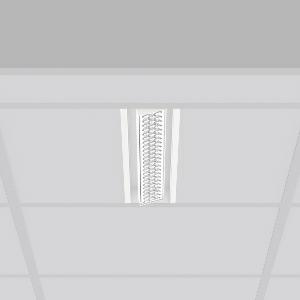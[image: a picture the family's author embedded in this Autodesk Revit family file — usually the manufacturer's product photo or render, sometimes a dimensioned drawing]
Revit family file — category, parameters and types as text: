
# Revit family: tx-move_901729_002_3_e311
name_source: partatom
category: Lighting Fixtures
units: mm (PartAtom-declared; Revit-internal decimal feet)

## family parameters
Cut with Voids When Loaded = No
Host = Face
Light Source = No
Part Type = Normal
Room Calculation Point = No
Round Connector Dimension = Use Diameter
Shared = No

## types (1)
- MultiLumen 1 (1 x LED Modul 835, 2950 lm, 3500)
    Apparent Load = 18 VA
    CIE Flux Codes = 77 96 99 100 100
    Color Rendering = 80
    Color Temperature = 3500
    Default Elevation = 1800 mm
    Description = Series: TX-MOVE
Einlege/Einbau-Flächenstrahler. Housing: sheet steel, powder-coated. Swivel range: 90°. High-efficiency LED units with optimum light control thanks to clear plastic (PC) lens optics. Spezielle Mikrostrukturen reduzieren Gelbsaum. Symmetrical light distribution. Suitable for laying in grid ceiling module 625. Connected converter included in separate gearbox.Suitable for through-wiring.MultiLumen: Luminous flux adjustable in 3 steps. Accessories: Mounting frame for installation in suspended ceilings. Environmentally friendly and resource-saving due to replaceable and recyclable components. 
Colour: traffic white, matt (RAL 9016)
Length: 622 mm
Width: 116 mm
Height: 39 mm
Cut-out length: 602 mm
Cut-out width: 98 mm
Recess height: 100 mm
Lamp: LED
Socket: without socket
Colour temperature: 3500K
Colour rendering index (CRI): 80
System power: 18 W
Rated luminous flux: 2950 lm
Luminous efficiency: 164 lm/W
System power 2: 26 W
Rated luminous flux 2: 4050 lm
Luminous efficiency 2: 156 lm/W
System power 3: 39 W
Rated luminous flux 3: 5700 lm
Luminous efficiency 3: 146 lm/W
Control gear: Regulated power supply
Protection class: I
Type of protection: IP 20
    Height = 0 mm  [stored 0 ft]
    Lamp = 1 x LED Modul 835
    Lamp Light Flux = 2950 lm
    Lamp count = 1
    Length = 622 mm
    Lifetime = 50000 h
    Luminous efficacy = 164 lm/W
    Manufacturer = RZB
    ModVariant = No
    Model = 901729.002.3
    Mounting Place = Ceiling, Wall
    Mounting Type = Recessed
    Number of Poles = 1
    OnlyDefault = Yes
    Power Factor = 1
    Product Name = TX-MOVE
    Product group = Recessed projectors
    ProductGroupID = 401
    Protection Class = Protection class I
    Protection Degree = IP 20
    RLX_Detail_Level = 1
    RLX_Emergency_Light_Flux = 0 lm
    RLX_Emergency_Type = 0
    RLX_Emergency_Type_DB = No
    RlxData = <blob elided: 27125 chars, md5=e6148af3>
    Socket = socket
    Standby Power = 0 W
    System Light Flux = 2950 lm
    System Power = 18 W
    Type Comments = MultiLumen 1
    Type Image = 901729.002.jpg
    URL = http://relux.com
    VarID = multilumen_1
    Voltage = 230 V
    Voltage Range = 220-240 V
    Weight = 0.00 kg
    Width = 116 mm

note: [stored X ft] marks values corroborated as IEEE doubles in the binary element streams (Revit-internal decimal feet)

## geometry (parser evidence)
native form markers: Blend x4, Sweep x15
no freeform markers — native parametric forms only
